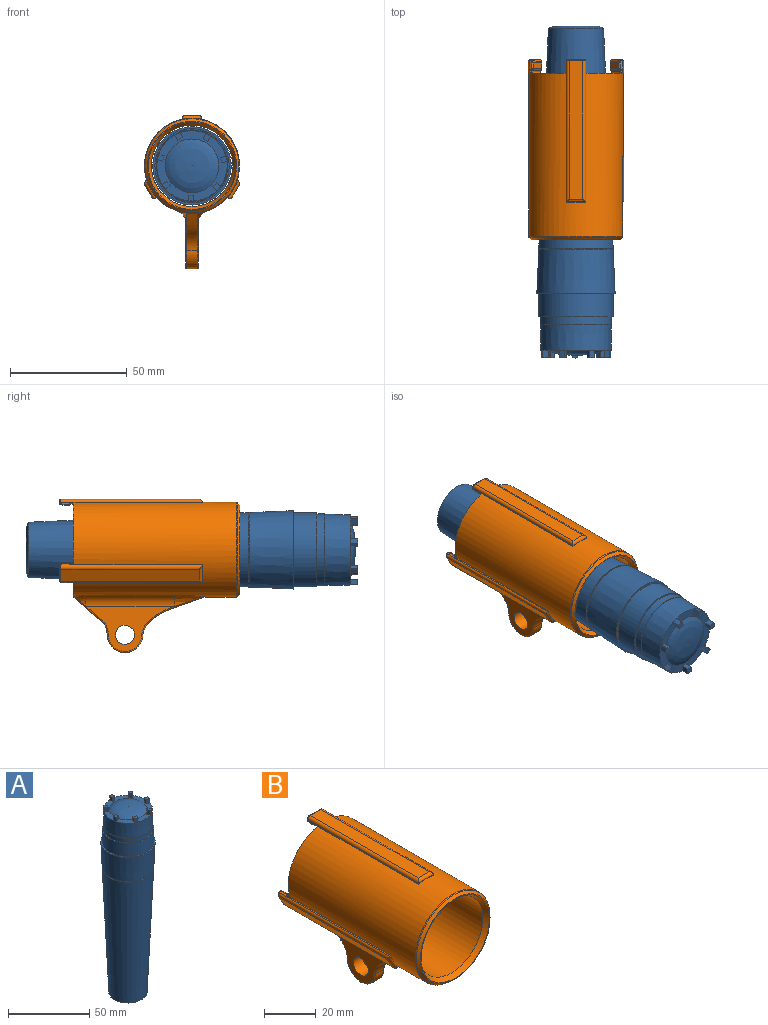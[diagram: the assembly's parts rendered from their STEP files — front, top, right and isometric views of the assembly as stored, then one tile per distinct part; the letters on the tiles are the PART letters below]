
ASSEMBLY  parts=2 mates=1
PART A: 60 faces, bbox 80.8x80.8x187.9 mm
  f0: cylinder r=12.58mm len=3.18mm, axis (0,0,1), area 7.3mm2, adj f1,f2,f4,f53
  f1: plane 3.18x1.89mm, normal (0.62,-0.78,0), area 7.7mm2, adj f0,f3,f4,f53
  f2: plane 3.18x1.89mm, normal (-0.62,0.78,0), area 7.7mm2, adj f0,f3,f4,f53
  f3: cylinder r=14.99mm len=3.18mm, axis (0,0,1), area 7.3mm2, adj f1,f2,f4,f53
  f4: plane 3.32x3.3mm, normal (0,0,1), area 5.5mm2, adj f0,f1,f2,f3
  f5: cylinder r=12.58mm len=3.18mm, axis (0,0,1), area 7.3mm2, adj f6,f7,f9,f53
  f6: plane 3.18x2.36mm, normal (-0.22,-0.97,0), area 7.7mm2, adj f5,f8,f9,f53
  f7: plane 3.18x2.36mm, normal (0.22,0.97,0), area 7.7mm2, adj f5,f8,f9,f53
  f8: cylinder r=14.99mm len=3.18mm, axis (0,0,1), area 7.3mm2, adj f6,f7,f9,f53
  f9: plane 2.87x2.77mm, normal (0,0,1), area 5.5mm2, adj f5,f6,f7,f8
  f10: cylinder r=12.58mm len=3.18mm, axis (0,0,1), area 7.3mm2, adj f11,f12,f14,f53
  f11: plane 3.18x2.18mm, normal (-0.9,-0.43,0), area 7.7mm2, adj f10,f13,f14,f53
  f12: plane 3.18x2.18mm, normal (0.9,0.43,0), area 7.7mm2, adj f10,f13,f14,f53
  f13: cylinder r=14.99mm len=3.18mm, axis (0,0,1), area 7.3mm2, adj f11,f12,f14,f53
  f14: plane 3.17x3.11mm, normal (0,0,1), area 5.5mm2, adj f10,f11,f12,f13
  f15: cylinder r=12.58mm len=3.18mm, axis (0,0,1), area 7.3mm2, adj f16,f17,f19,f53
  f16: plane 3.18x2.18mm, normal (-0.9,0.43,0), area 7.7mm2, adj f15,f18,f19,f53
  f17: plane 3.18x2.18mm, normal (0.9,-0.43,0), area 7.7mm2, adj f15,f18,f19,f53
  f18: cylinder r=14.99mm len=3.18mm, axis (0,0,1), area 7.3mm2, adj f16,f17,f19,f53
  f19: plane 3.17x3.11mm, normal (0,0,1), area 5.5mm2, adj f15,f16,f17,f18
  f20: cylinder r=12.58mm len=3.18mm, axis (0,0,1), area 7.3mm2, adj f21,f22,f24,f53
  f21: plane 3.18x2.36mm, normal (-0.22,0.97,0), area 7.7mm2, adj f20,f23,f24,f53
  f22: plane 3.18x2.36mm, normal (0.22,-0.97,0), area 7.7mm2, adj f20,f23,f24,f53
  f23: cylinder r=14.99mm len=3.18mm, axis (0,0,1), area 7.3mm2, adj f21,f22,f24,f53
  f24: plane 2.87x2.77mm, normal (0,0,1), area 5.5mm2, adj f20,f21,f22,f23
  f25: cylinder r=12.58mm len=3.18mm, axis (0,0,1), area 7.3mm2, adj f26,f27,f29,f53
  f26: plane 3.18x1.89mm, normal (0.62,0.78,0), area 7.7mm2, adj f25,f28,f29,f53
  f27: plane 3.18x1.89mm, normal (-0.62,-0.78,0), area 7.7mm2, adj f25,f28,f29,f53
  f28: cylinder r=14.99mm len=3.18mm, axis (0,0,1), area 7.3mm2, adj f26,f27,f29,f53
  f29: plane 3.32x3.3mm, normal (0,0,1), area 5.5mm2, adj f25,f26,f27,f28
  f30: cone r=15.24mm half-angle=1deg, axis (0,0,-1), area 1051.5mm2, adj f43,f53
  f31: cone r=16.76mm half-angle=2.5deg, axis (0,0,1), area 8205.7mm2, adj f36,f37
  f32: plane 18.47x18.47mm, normal (0,0,-1), area 59.5mm2, adj f33,f35,f36
  f33: cylinder r=8.06mm len=16.13mm, axis (0,0,-1), area 596.5mm2, adj f32,f34,f35
  f34: plane 16.13x16.13mm, normal (0,0,-1), area 196.5mm2, adj f33,f35,f44,f46,f48
  f35: cylinder r=1.84mm len=12.7mm, axis (0,0,-1), area 75.2mm2, adj f32,f33,f34,f36
  f36: cone r=11.81mm half-angle=70deg, axis (0,0,1), area 181.6mm2, adj f31,f32,f35
  f37: torus R=15.93mm, axis (0,0,1), area 79.4mm2, adj f31,f39
  f38: plane 33.53x33.53mm, normal (0,0,1), area 91.2mm2, adj f39,f40
  f39: cone r=16.76mm half-angle=2.5deg, axis (0,0,1), area 1930.9mm2, adj f37,f38
  f40: cylinder r=15.88mm len=31.75mm, axis (0,0,-1), area 1013.4mm2, adj f38,f41
  f41: plane 31.75x31.75mm, normal (0,0,1), area 49.9mm2, adj f40,f42
  f42: cylinder r=15.37mm len=30.73mm, axis (0,0,-1), area 318.8mm2, adj f41,f43
  f43: plane 30.73x30.73mm, normal (0,0,1), area 12.2mm2, adj f30,f42
  f44: cylinder r=1.17mm len=9.53mm, axis (0,0,1), area 69.9mm2, adj f34,f52
  f45: plane 1.07x1.07mm, normal (0,0,-1), area 0.9mm2, adj f52
  f46: cylinder r=1.17mm len=9.53mm, axis (0,0,1), area 69.9mm2, adj f34,f51
  f47: plane 1.07x1.07mm, normal (0,0,-1), area 0.9mm2, adj f51
  f48: cylinder r=1.17mm len=9.53mm, axis (0,0,1), area 69.9mm2, adj f34,f50
  f49: plane 1.07x1.07mm, normal (0,0,-1), area 0.9mm2, adj f50
  f50: bspline ~2.34x2.34mm, area 6.2mm2, adj f48,f49
  f51: bspline ~2.34x2.34mm, area 6.2mm2, adj f46,f47
  f52: bspline ~2.34x2.34mm, area 6.2mm2, adj f44,f45
  f53: plane 76.05x76.05mm, normal (0,0,1), area 257.9mm2, adj f0,f1,f2,f3,f5,f6,f7,f8
  f54: cylinder r=12.58mm len=3.18mm, axis (0,0,1), area 7.3mm2, adj f53,f55,f57,f58
  f55: plane 3.18x2.42mm, normal (-1,0,0), area 7.7mm2, adj f53,f54,f56,f58
  f56: cylinder r=14.99mm len=3.18mm, axis (0,0,1), area 7.3mm2, adj f53,f55,f57,f58
  f57: plane 3.18x2.42mm, normal (1,0,0), area 7.7mm2, adj f53,f54,f56,f58
  f58: plane 2.47x2.29mm, normal (0,0,1), area 5.5mm2, adj f54,f55,f56,f57
  f59: revolved ~22.97x22.95mm, area 0mm2, adj f53
PART B: 130 faces, bbox 42.3x77.6x67 mm
  f0: plane 3.65x2.49mm, normal (0,-1,0), area 0.6mm2, adj f3,f44,f55
  f1: plane 6.58x3.8mm, normal (-0.87,0,0.5), area 0.1mm2, adj f4,f49,f57,f73
  f2: plane 60.45x0.66mm, normal (0.5,0,0.87), area 27.3mm2, adj f3,f46,f54,f67,f68,f69,f70,f71
  f3: cylinder r=20.32mm len=69.6mm, axis (0,1,0), area 6514.6mm2, adj f0,f2,f4,f5,f7,f8,f10,f13
  f4: plane 41.04x40.6mm, normal (0,1,0), area 318.7mm2, adj f1,f3,f6,f9,f11,f57,f73,f74
  f5: plane 3.87x2.11mm, normal (0,-1,0), area 0.6mm2, adj f3,f31,f42
  f6: plane 6.58x3.8mm, normal (0.87,0,0.5), area 0.1mm2, adj f4,f36,f74,f90
  f7: plane 60.45x0.66mm, normal (0.5,0,-0.87), area 27.3mm2, adj f3,f33,f41,f84,f85,f86,f87,f88
  f8: plane 4.22x0.44mm, normal (0,-1,0), area 0.6mm2, adj f3,f18,f29
  f9: plane 7.6x0.01mm, normal (0,0,-1), area 0.1mm2, adj f4,f23,f91,f107
  f10: plane 60.45x0.76mm, normal (-1,0,0), area 27.3mm2, adj f3,f20,f28,f101,f102,f103,f104,f105
  f11: cylinder r=17.4mm len=68.92mm, axis (0,1,0), area 7534.4mm2, adj f4,f15
  f12: plane 38.1x38.1mm, normal (0,-1,0), area 45.1mm2, adj f15,f16
  f13: plane 35.34x8.73mm, normal (1,0,0), area 279.2mm2, adj f3,f14,f16,f17
  f14: plane 8.09x0.41mm, normal (0,-1,0), area 2.2mm2, adj f3,f13
  f15: cone r=17.4mm half-angle=30deg, axis (0,-1,0), area 287.8mm2, adj f11,f12
  f16: cone r=19.05mm half-angle=45deg, axis (0,1,0), area 189.9mm2, adj f12,f13,f17
  f17: cone r=20.32mm half-angle=22.5deg, axis (0,1,0), area 56.3mm2, adj f3,f13,f16
  f18: plane 60.45x0.76mm, normal (1,0,0), area 27.3mm2, adj f3,f8,f30,f91,f92,f93,f94,f95
  f19: plane 7.42x2.54mm, normal (0,0,-1), area 18.8mm2, adj f24,f27,f93,f105
  f20: plane 4.22x0.44mm, normal (0,-1,0), area 0.6mm2, adj f3,f10,f29
  f21: plane 7.42x1.26mm, normal (0,1,0), area 9.1mm2, adj f26,f97,f98,f99,f100,f101
  f22: plane 59.18x5.89mm, normal (0,0,1), area 348.7mm2, adj f28,f29,f30,f99
  f23: cylinder r=0.74mm len=7.42mm, axis (-1,0,0), area 14.6mm2, adj f9,f24,f91,f107
  f24: cylinder r=0.64mm len=7.42mm, axis (-1,0,0), area 5.1mm2, adj f19,f23,f92,f106
  f25: plane 7.42x0.7mm, normal (0,0.2,-0.98), area 5.3mm2, adj f26,f27,f95,f103
  f26: cylinder r=0.64mm len=7.42mm, axis (-1,0,0), area 6.5mm2, adj f21,f25,f96,f102
  f27: cylinder r=0.64mm len=7.42mm, axis (-1,0,0), area 0.9mm2, adj f19,f25,f94,f104
  f28: cylinder r=1.27mm len=60.45mm, axis (0,1,0), area 119.3mm2, adj f10,f22,f29,f100
  f29: cylinder r=1.27mm len=8.43mm, axis (-1,0,0), area 14.3mm2, adj f8,f20,f22,f28,f30
  f30: cylinder r=1.27mm len=60.45mm, axis (0,-1,0), area 119.3mm2, adj f18,f22,f29,f98
  f31: plane 60.45x0.66mm, normal (-0.5,0,0.87), area 27.3mm2, adj f3,f5,f43,f74,f75,f76,f77,f78
  f32: plane 6.42x3.71mm, normal (0.87,0,0.5), area 18.8mm2, adj f37,f40,f76,f88
  f33: plane 3.65x2.49mm, normal (0,-1,0), area 0.6mm2, adj f3,f7,f42
  f34: plane 6.77x4.52mm, normal (0,1,0), area 9.1mm2, adj f39,f80,f81,f82,f83,f84
  f35: plane 59.18x5.1mm, normal (-0.87,0,-0.5), area 348.7mm2, adj f41,f42,f43,f82
  f36: cylinder r=0.74mm len=6.79mm, axis (0.5,0,-0.87), area 14.6mm2, adj f6,f37,f74,f90
  f37: cylinder r=0.64mm len=6.59mm, axis (0.5,0,-0.87), area 5.1mm2, adj f32,f36,f75,f89
  f38: plane 6.49x3.83mm, normal (0.85,0.2,0.49), area 5.3mm2, adj f39,f40,f78,f86
  f39: cylinder r=0.64mm len=6.73mm, axis (0.5,0,-0.87), area 6.5mm2, adj f34,f38,f79,f85
  f40: cylinder r=0.64mm len=6.43mm, axis (0.5,0,-0.87), area 0.9mm2, adj f32,f38,f77,f87
  f41: cylinder r=1.27mm len=60.45mm, axis (0,1,0), area 119.3mm2, adj f7,f35,f42,f83
  f42: cylinder r=1.27mm len=7.94mm, axis (0.5,0,-0.87), area 14.3mm2, adj f5,f33,f35,f41,f43
  f43: cylinder r=1.27mm len=60.45mm, axis (0,-1,0), area 119.3mm2, adj f31,f35,f42,f81
  f44: plane 60.45x0.66mm, normal (-0.5,0,-0.87), area 27.3mm2, adj f0,f3,f56,f57,f58,f59,f60,f61
  f45: plane 6.42x3.71mm, normal (-0.87,0,0.5), area 18.8mm2, adj f50,f53,f59,f71
  f46: plane 3.87x2.11mm, normal (0,-1,0), area 0.6mm2, adj f2,f3,f55
  f47: plane 6.77x4.52mm, normal (0,1,0), area 9.1mm2, adj f52,f63,f64,f65,f66,f67
  f48: plane 59.18x5.1mm, normal (0.87,0,-0.5), area 348.7mm2, adj f54,f55,f56,f65
  f49: cylinder r=0.74mm len=6.79mm, axis (0.5,0,0.87), area 14.6mm2, adj f1,f50,f57,f73
  f50: cylinder r=0.64mm len=6.59mm, axis (0.5,0,0.87), area 5.1mm2, adj f45,f49,f58,f72
  f51: plane 6.49x3.83mm, normal (-0.85,0.2,0.49), area 5.3mm2, adj f52,f53,f61,f69
  f52: cylinder r=0.64mm len=6.73mm, axis (0.5,0,0.87), area 6.5mm2, adj f47,f51,f62,f68
  f53: cylinder r=0.64mm len=6.43mm, axis (0.5,0,0.87), area 0.9mm2, adj f45,f51,f60,f70
  f54: cylinder r=1.27mm len=60.45mm, axis (0,1,0), area 119.3mm2, adj f2,f48,f55,f66
  f55: cylinder r=1.27mm len=7.94mm, axis (0.5,0,0.87), area 14.3mm2, adj f0,f46,f48,f54,f56
  f56: cylinder r=1.27mm len=60.45mm, axis (0,-1,0), area 119.3mm2, adj f44,f48,f55,f64
  f57: torus R=1.25mm, axis (-0.5,0,-0.87), area 1.6mm2, adj f1,f3,f4,f44,f49,f58
  f58: torus R=0.13mm, axis (-0.5,0,-0.87), area 0.4mm2, adj f44,f50,f57,f59
  f59: cylinder r=0.51mm len=2.54mm, axis (0,1,0), area 2mm2, adj f44,f45,f58,f60
  f60: torus R=0.13mm, axis (-0.5,0,-0.87), area 0.1mm2, adj f44,f53,f59,f61
  f61: cylinder r=0.51mm len=0.8mm, axis (0.17,0.98,-0.1), area 0.6mm2, adj f44,f51,f60,f62
  f62: torus R=0.13mm, axis (-0.5,0,-0.87), area 0.5mm2, adj f44,f52,f61,f63
  f63: cylinder r=0.51mm len=0.69mm, axis (-0.87,0,0.5), area 0.4mm2, adj f44,f47,f62,f64
  f64: torus R=0.76mm, axis (0,1,0), area 1.4mm2, adj f47,f56,f63,f65
  f65: cylinder r=0.51mm len=5.36mm, axis (-0.5,0,-0.87), area 4.7mm2, adj f47,f48,f64,f66
  f66: torus R=0.76mm, axis (0,1,0), area 1.4mm2, adj f47,f54,f65,f67
  f67: cylinder r=0.51mm len=0.69mm, axis (0.87,0,-0.5), area 0.4mm2, adj f2,f47,f66,f68
  f68: torus R=0.13mm, axis (-0.5,0,-0.87), area 0.5mm2, adj f2,f52,f67,f69
  f69: cylinder r=0.51mm len=0.81mm, axis (0.17,0.98,-0.1), area 0.6mm2, adj f2,f51,f68,f70
  f70: torus R=0.13mm, axis (-0.5,0,-0.87), area 0.1mm2, adj f2,f53,f69,f71
  f71: cylinder r=0.51mm len=2.54mm, axis (0,-1,0), area 2mm2, adj f2,f45,f70,f72
  f72: torus R=0.13mm, axis (-0.5,0,-0.87), area 0.4mm2, adj f2,f50,f71,f73
  f73: torus R=1.25mm, axis (-0.5,0,-0.87), area 1.6mm2, adj f1,f2,f3,f4,f49,f72
  f74: torus R=1.25mm, axis (-0.5,0,0.87), area 1.6mm2, adj f3,f4,f6,f31,f36,f75
  f75: torus R=0.13mm, axis (-0.5,0,0.87), area 0.4mm2, adj f31,f37,f74,f76
  f76: cylinder r=0.51mm len=2.54mm, axis (0,1,0), area 2mm2, adj f31,f32,f75,f77
  f77: torus R=0.13mm, axis (-0.5,0,0.87), area 0.1mm2, adj f31,f40,f76,f78
  f78: cylinder r=0.51mm len=0.81mm, axis (-0.17,0.98,-0.1), area 0.6mm2, adj f31,f38,f77,f79
  f79: torus R=0.13mm, axis (-0.5,0,0.87), area 0.5mm2, adj f31,f39,f78,f80
  f80: cylinder r=0.51mm len=0.69mm, axis (0.87,0,0.5), area 0.4mm2, adj f31,f34,f79,f81
  f81: torus R=0.76mm, axis (0,1,0), area 1.4mm2, adj f34,f43,f80,f82
  f82: cylinder r=0.51mm len=5.36mm, axis (-0.5,0,0.87), area 4.7mm2, adj f34,f35,f81,f83
  f83: torus R=0.76mm, axis (0,1,0), area 1.4mm2, adj f34,f41,f82,f84
  f84: cylinder r=0.51mm len=0.69mm, axis (-0.87,0,-0.5), area 0.4mm2, adj f7,f34,f83,f85
  f85: torus R=0.13mm, axis (-0.5,0,0.87), area 0.5mm2, adj f7,f39,f84,f86
  f86: cylinder r=0.51mm len=0.8mm, axis (-0.17,0.98,-0.1), area 0.6mm2, adj f7,f38,f85,f87
  f87: torus R=0.13mm, axis (-0.5,0,0.87), area 0.1mm2, adj f7,f40,f86,f88
  f88: cylinder r=0.51mm len=2.54mm, axis (0,-1,0), area 2mm2, adj f7,f32,f87,f89
  f89: torus R=0.13mm, axis (-0.5,0,0.87), area 0.4mm2, adj f7,f37,f88,f90
  f90: torus R=1.25mm, axis (-0.5,0,0.87), area 1.6mm2, adj f3,f4,f6,f7,f36,f89
  f91: torus R=1.25mm, axis (1,0,0), area 1.6mm2, adj f3,f4,f9,f18,f23,f92
  f92: torus R=0.13mm, axis (1,0,0), area 0.4mm2, adj f18,f24,f91,f93
  f93: cylinder r=0.51mm len=2.54mm, axis (0,1,0), area 2mm2, adj f18,f19,f92,f94
  f94: torus R=0.13mm, axis (1,0,0), area 0.1mm2, adj f18,f27,f93,f95
  f95: cylinder r=0.51mm len=0.8mm, axis (0,0.98,0.2), area 0.6mm2, adj f18,f25,f94,f96
  f96: torus R=0.13mm, axis (1,0,0), area 0.5mm2, adj f18,f26,f95,f97
  f97: cylinder r=0.51mm len=0.51mm, axis (0,0,-1), area 0.4mm2, adj f18,f21,f96,f98
  f98: torus R=0.76mm, axis (0,1,0), area 1.4mm2, adj f21,f30,f97,f99
  f99: cylinder r=0.51mm len=5.89mm, axis (1,0,0), area 4.7mm2, adj f21,f22,f98,f100
  f100: torus R=0.76mm, axis (0,1,0), area 1.4mm2, adj f21,f28,f99,f101
  f101: cylinder r=0.51mm len=0.51mm, axis (0,0,1), area 0.4mm2, adj f10,f21,f100,f102
  f102: torus R=0.13mm, axis (1,0,0), area 0.5mm2, adj f10,f26,f101,f103
  f103: cylinder r=0.51mm len=0.8mm, axis (0,0.98,0.2), area 0.6mm2, adj f10,f25,f102,f104
  f104: torus R=0.13mm, axis (1,0,0), area 0.1mm2, adj f10,f27,f103,f105
  f105: cylinder r=0.51mm len=2.54mm, axis (0,-1,0), area 2mm2, adj f10,f19,f104,f106
  f106: torus R=0.13mm, axis (1,0,0), area 0.4mm2, adj f10,f24,f105,f107
  f107: torus R=1.25mm, axis (1,0,0), area 1.6mm2, adj f3,f4,f9,f10,f23,f106
  f108: extruded ~25.5x15.86mm, area 135.8mm2, adj f112,f114,f116,f125
  f109: extruded ~15.13x12.99mm, area 88.9mm2, adj f112,f115,f117,f124
  f110: plane 37.8x19.3mm, normal (1,0,0), area 296.2mm2, adj f113,f116,f117,f119,f129
  f111: plane 37.8x19.3mm, normal (-1,0,0), area 296.2mm2, adj f113,f114,f115,f118,f121
  f112: cylinder r=7.62mm len=15.24mm, axis (-1,0,0), area 103.4mm2, adj f108,f109,f118,f119
  f113: cylinder r=4.06mm len=8.13mm, axis (-1,0,0), area 136.2mm2, adj f110,f111
  f114: bspline ~27.18x16.97mm, area 22.1mm2, adj f108,f111,f118,f123
  f115: bspline ~16.5x14.24mm, area 15.2mm2, adj f109,f111,f118,f120,f122
  f116: bspline ~27.19x17.04mm, area 22.1mm2, adj f108,f110,f119,f127
  f117: bspline ~16.5x14.24mm, area 15.2mm2, adj f109,f110,f119,f126,f128
  f118: torus R=7.11mm, axis (1,0,0), area 18.7mm2, adj f111,f112,f114,f115
  f119: torus R=7.11mm, axis (1,0,0), area 18.7mm2, adj f110,f112,f116,f117
  f120: bspline ~7.39x5.53mm, area 20.5mm2, adj f3,f115,f121,f122
  f121: cylinder r=5.08mm len=37.79mm, axis (0,1,0), area 242.1mm2, adj f3,f111,f120,f123
  f122: bspline ~3.62x2.66mm, area 4.5mm2, adj f4,f115,f120,f124
  f123: bspline ~16.17x5.56mm, area 56mm2, adj f3,f114,f121,f125
  f124: bspline ~4.32x1.62mm, area 7.5mm2, adj f4,f109,f122,f126
  f125: bspline ~7.12x2.39mm, area 6.8mm2, adj f3,f108,f123,f127
  f126: bspline ~3.11x2.52mm, area 4.5mm2, adj f4,f117,f124,f128
  f127: bspline ~16.17x5.56mm, area 56mm2, adj f3,f116,f125,f129
  f128: bspline ~7.13x5.53mm, area 20.5mm2, adj f3,f117,f126,f129
  f129: cylinder r=5.08mm len=37.79mm, axis (0,1,0), area 242.1mm2, adj f3,f110,f127,f128
PLACE A rot(axis=(0.96,-0.2,0.2),92.5deg) t=(-5.97,-71.11,1.79)mm
PLACE B t=(-5.97,22.92,1.79)mm fixed
MATE cylindrical A.f0 <-> B.f3  axis (0,1,0) through (-5.97,-76.19,1.79)mm
